# Revit family: IS_UltraFlat_K1634_BIM_DE
name_source: partatom
category: Plumbing Fixtures
revit_build: Autodesk Revit MEP 2016 (Build: 20161004_0715(x64)
units: mm (PartAtom-declared; Revit-internal decimal feet)

## family parameters
Always vertical = No
Cut with Voids When Loaded = No
OmniClass Number = 23.45.05.14.21.11
OmniClass Title = Bath/Shower Units
Part Type = Normal
Room Calculation Point = No
Round Connector Dimension = Use Diameter
Shared = No
Work Plane-Based = No

## types (2) — shared parameters
Accessories = www.idealstandard.de\ersatzteile
AssetType = Fixed
BIMobject category = Shower trays
BOSUseNativeGeometries = 1
Brand = Ideal Standard
Brand url = http://www.idealstandard.de
CodePerformance = DIN EN 14527, DIN EN 249
ConnectionType = Plumbing
CurrencyUnit = €
CurrentRevision = 1
Date of publishing = 20/12/2017
DurationUnit = Year
Edition number = 1
ExpectedLife = 25
IFC Classification = Sanitary Terminal
IfcExportAs = IfcSanitaryTerminalType
Installation instructions = http://www.idealstandard.de
InstallationInstructions = www.idealstandard.de\produkte
MaintenanceInformation = www.idealstandard.de\produkte
Manufacturer name = Ideal Standard
ManufacturerURL = http://www.idealstandard.de
Material = Sanitary Brass
Material main = Acrylic
NBS Reference Code = 35-06-84
NBS Reference Description = Shower Trays
NettWeight = 31 Kg
Nominal height = 140
Nominal width = 900
NominalDepth = 900 mm
NominalHeight = 40 mm
NominalLength = 900 mm
NominalWidth = 1600 mm
OmniClass Code = 23-31 17 00
OmniClass Description = Showers
Product Guid = edfea03c-cd67-4d1c-96ef-27612eb29f41
Product SKU = K1634
Product data url = https://bimobject.com
Product family = Sanitary
Product group = Shower Tray
Product name = ULTRA FLAT rectangular shower tray 1600x900mm
Product url = http://www.idealstandard.de
ProductInformation = www.idealstandard.de/produkte
QR code = http://bimobject.com
Shape = Rectangular
Size = 40 x 900 x 1600mm
Space = Internal
SpareParts = www.idealstandard.de/ersatzteile
Technical description = http://www.idealstandard.de
URL = http://www.idealstandard.de
Uniclass 1.4 Code = L7214
Uniclass 1.4 Description = Showers
Uniclass 2.0 Code = PR-35-06-84
Uniclass 2.0 Description = Shower Trays
Uniclass 2015 Code = Pr_40_20_06_84
Uniclass 2015 Name = Shower trays
Uniclass2015Code = Pr_40_20_06_84
Uniclass2015Title = Shower trays
Uniclass2015Version = Products v1.1
Version = 1
VolumeUnits = Litres
Weight Net (Kg) = 31
zero-valued in all types: Cost, DrainSize, MaterialThickness

## per-type parameters (varying)
| type | BIMObjectName | BarCode | Color | Description | EAN code | Features | Finish | MainColor | Model | ModelNumber | ModelReference | Name |
| K163401 - ULTRA FLAT rectangular shower tray 1600x900mm | ISI_IdealStandard_ShowerTrays_UltraFlat_K163401 | 4015413019316 | White | IS Rechteck-Brausewanne ULTRA FLAT, 1600x900x140mm, Weiß | https://4015413019316 | IS Rechteck-Brausewanne ULTRA FLAT, 1600x900x140mm, Weiß | White | White | K163401 | K163401 | IS Rechteck-Brausewanne ULTRA FLAT, 1600x900x140mm, Weiß | ShowerTrays_UltraFlat_K163401 |
| K1634YK - ULTRA FLAT rectangular shower tray 1600x900mm | ISI_IdealStandard_ShowerTrays_UltraFlat_K1634YK | 4015413035637 | White Ideal Grip | IS Rechteck-Brausewanne ULTRA FLAT, 1600x900x140mm, Weiß mit Ideal Grip | https://4015413035637 | IS Rechteck-Brausewanne ULTRA FLAT, 1600x900x140mm, Weiß mit Ideal Grip | White Ideal Grip | White Ideal Grip | K1634YK | K1634YK | IS Rechteck-Brausewanne ULTRA FLAT, 1600x900x140mm, Weiß mit Ideal Grip | ShowerTrays_UltraFlat_K1634YK |

## geometry (parser evidence)
native form markers: Blend x4, Sweep x2
no freeform markers — native parametric forms only
